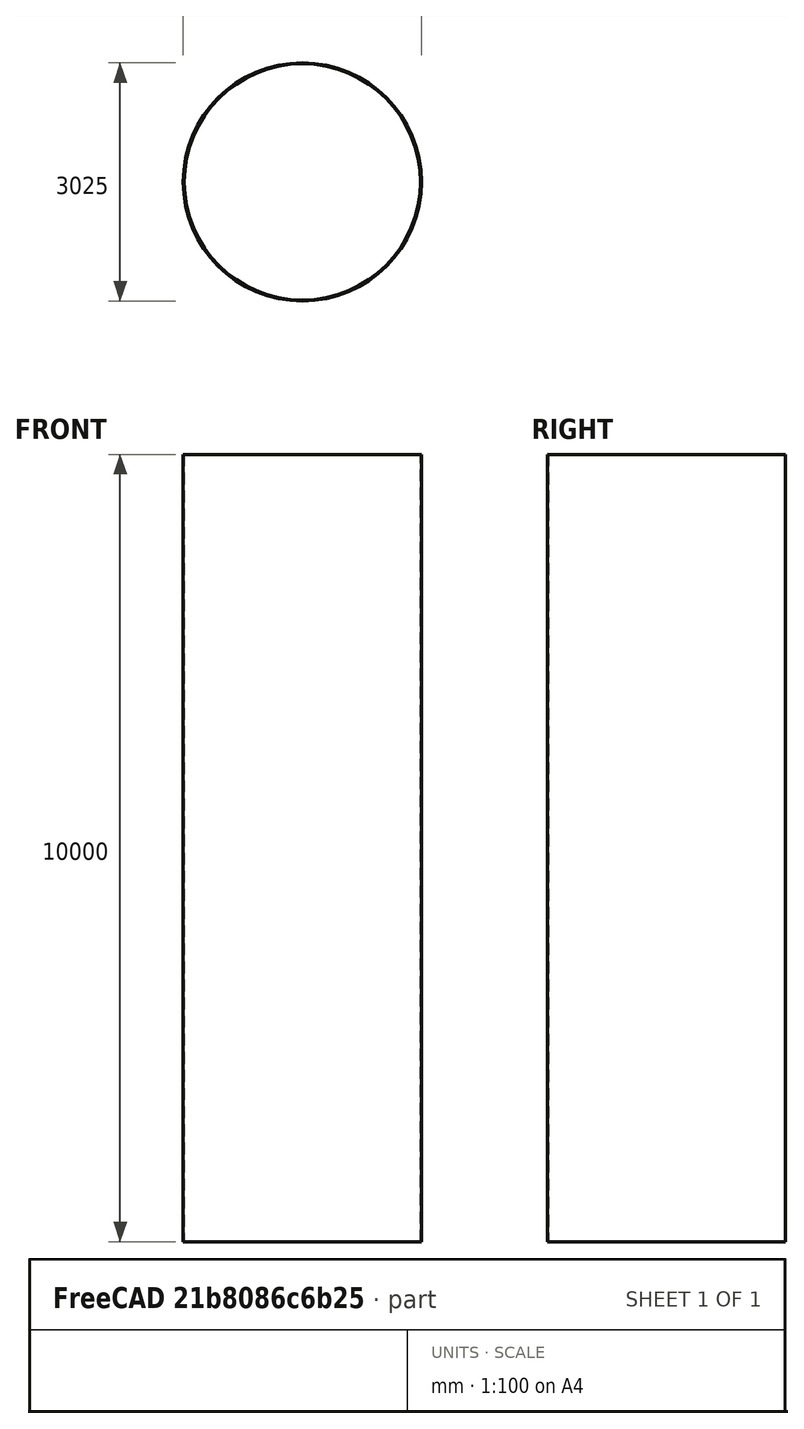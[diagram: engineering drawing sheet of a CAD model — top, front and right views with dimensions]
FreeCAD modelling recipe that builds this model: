
FCSTD DOCUMENT  (FreeCAD 0.21R33771 (Git))
Label: part2(capsule)
License: All rights reserved
LicenseURL: http://en.wikipedia.org/wiki/All_rights_reserved
objects: Sketcher::SketchObject×1, PartDesign::Pad×1, PartDesign::Body×1
note: 4 computed .brp shape members not serialized (recipe doc carries the construction recipe); baked Part::Feature solids carry a one-line shape summary decoded from their .brp

FEATURE [Sketcher::SketchObject] Sketch
  FullyConstrained = true
  MapMode = 5
  Support = -> [XY_Plane]
  sketch-geometry (2):
    g0: Circle CenterX=0 CenterY=0 CenterZ=0 NormalX=0 NormalY=0 NormalZ=1 AngleXU=0 Radius=1500
    g1: Circle CenterX=0 CenterY=0 CenterZ=0 NormalX=0 NormalY=0 NormalZ=1 AngleXU=0 Radius=1512.5
  constraints (4):
    c: Coincident(g0,g-1)
    c: Coincident(g1,g0)
    c: Diameter(g0) = 3000
    c: Diameter(g1) = 3025
FEATURE [PartDesign::Pad] Pad
  Direction = (0,0,1)
  Length = 10000
  Length2 = 10
  Profile = -> Sketch
  ReferenceAxis = -> Sketch [N_Axis]
  Type = 0
FEATURE [PartDesign::Body] Body
  Group = -> [Sketch,Pad]
  Origin = -> Origin
  Tip = -> Pad
